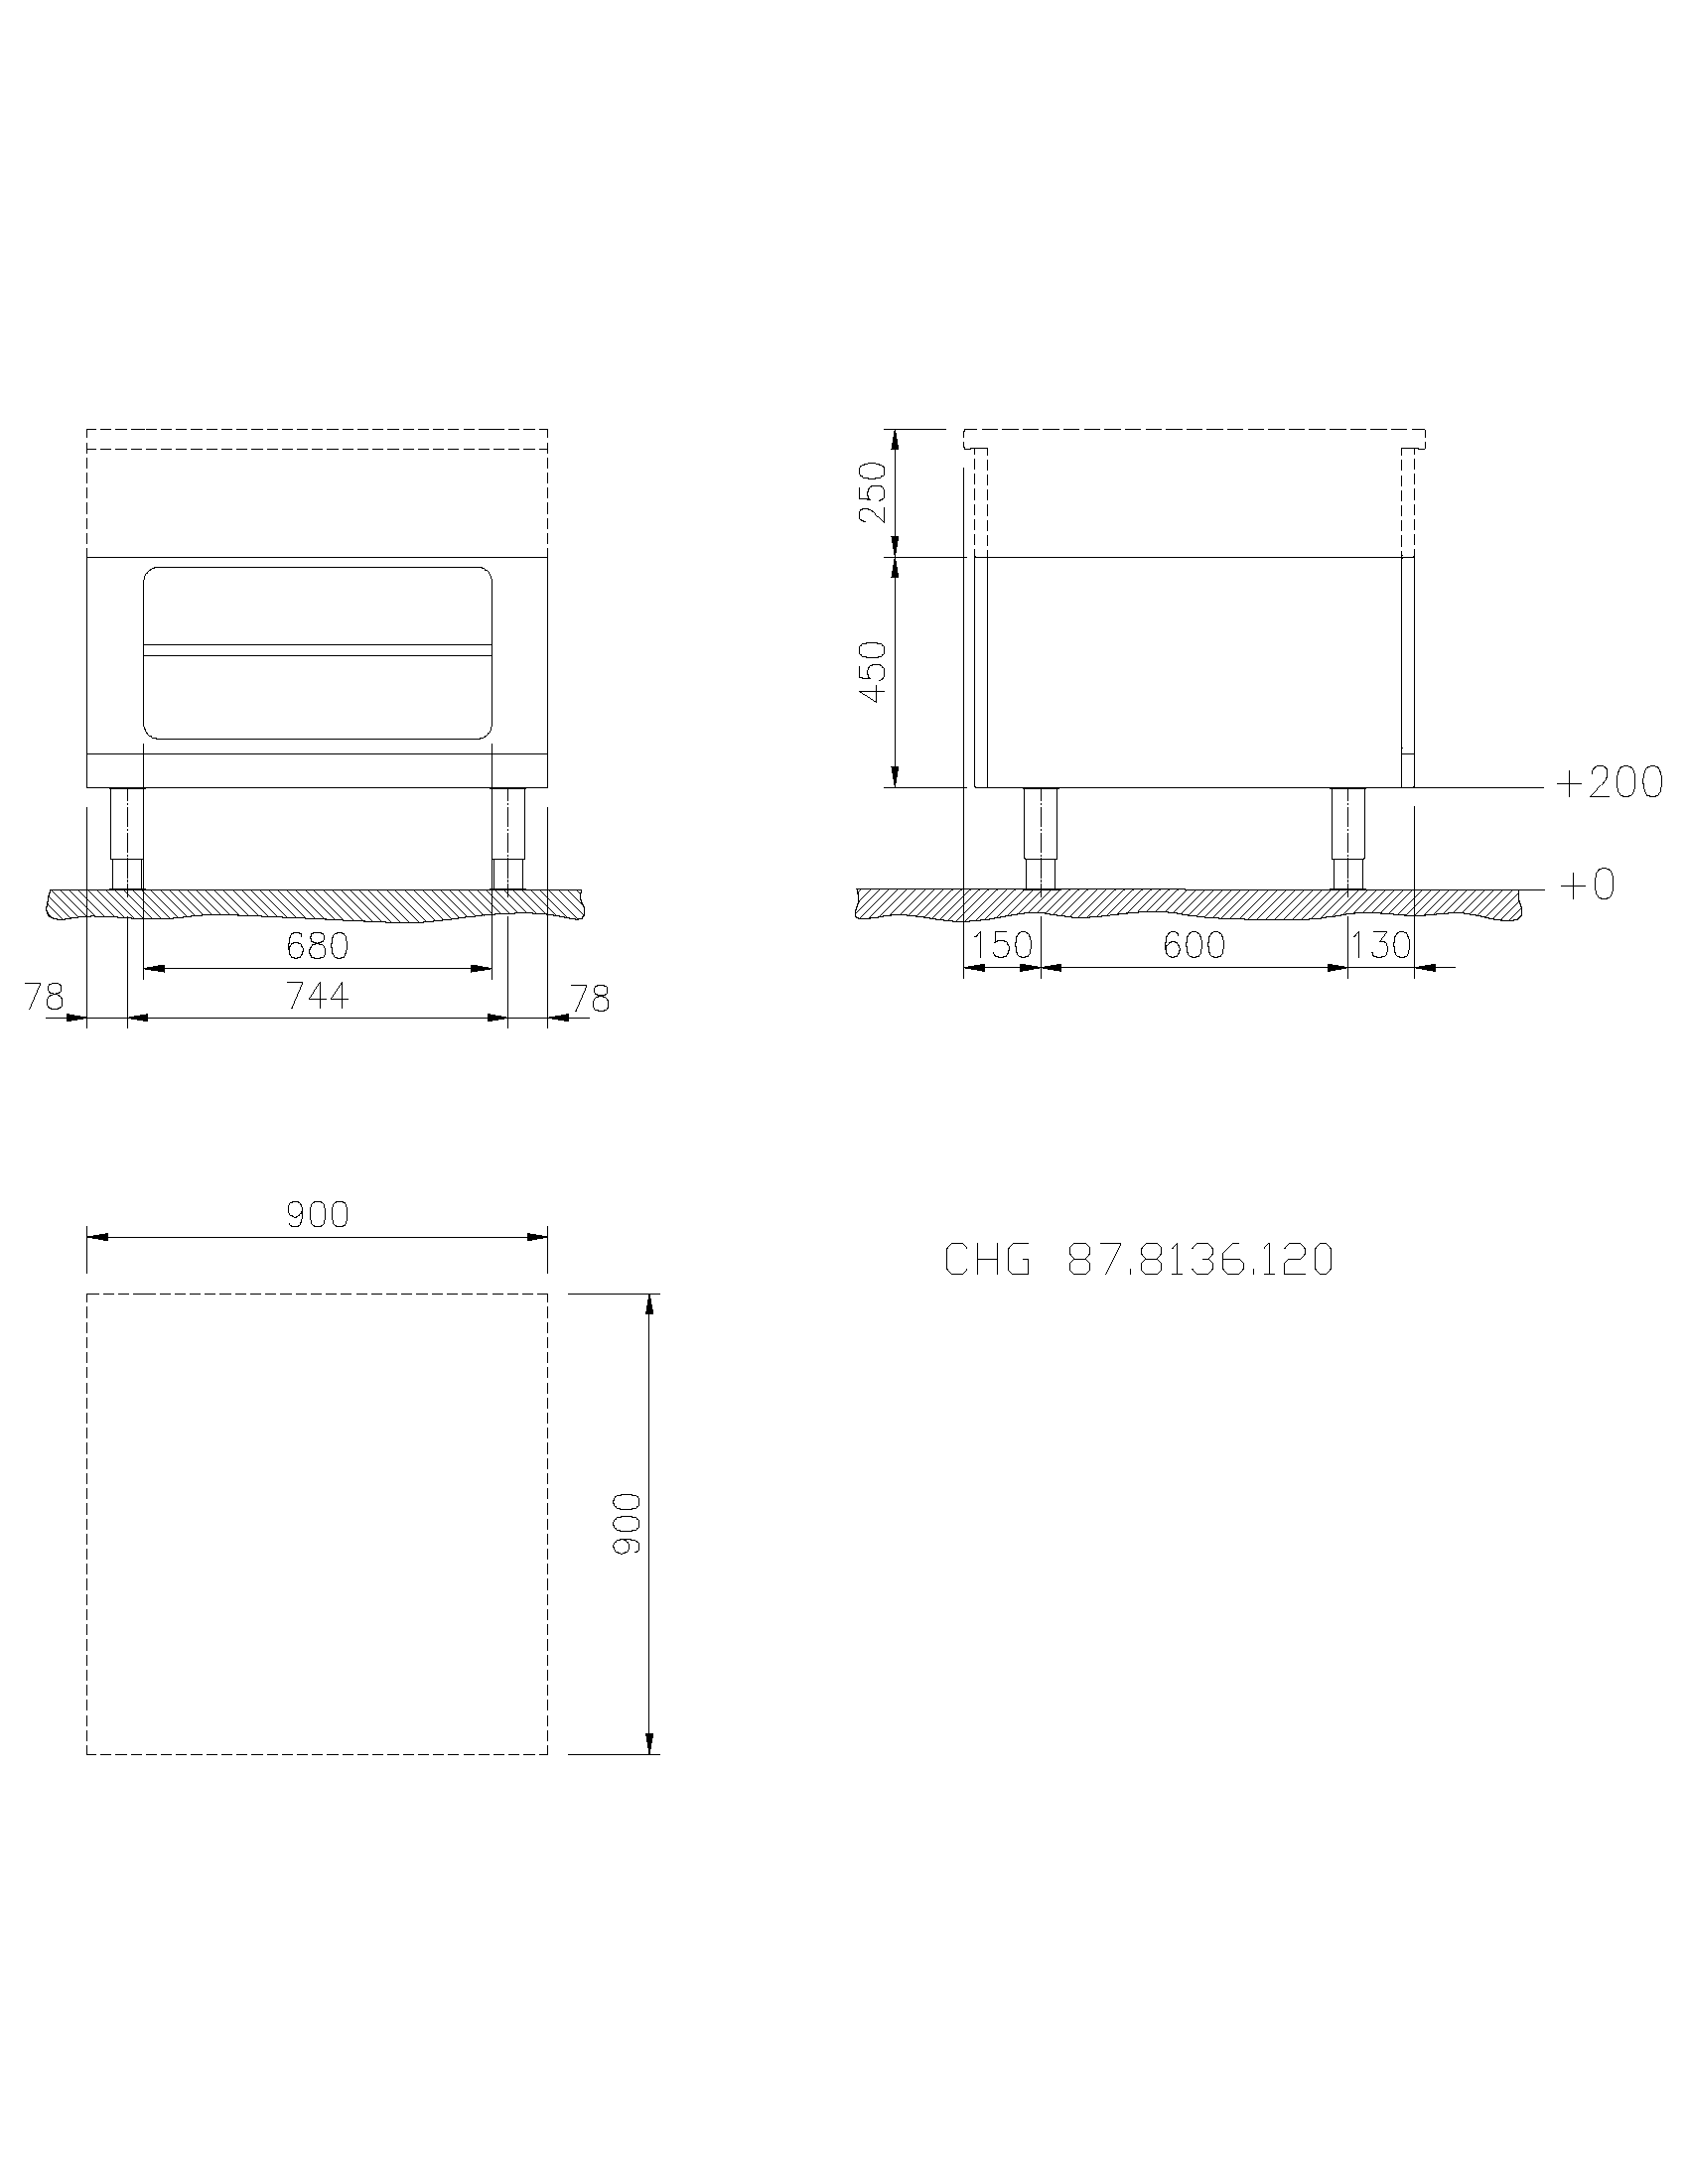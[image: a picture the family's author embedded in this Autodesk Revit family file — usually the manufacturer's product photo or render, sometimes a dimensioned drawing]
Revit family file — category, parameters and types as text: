
# Revit family: QF_ELECTROLUXPROFESSIONAL_589838_MCHZEAD1DM
name_source: partatom
category: Attrezzature speciali
units: mm (PartAtom-declared; Revit-internal decimal feet)

## family parameters
Basato su piano di lavoro = No
Condiviso = No
Punto di calcolo locali = No
Quota connettore circolare = Usa diametro
Sempre verticale = Sì
Taglio con vuoti quando caricato = No
Tipo di parte = Normale

## types (1)
- Standard
    Accessory = Sì
    Cold Water Size = 0"
    Compressed Air Pressure = 0.00 psi
    Compressed Air Size = 0"
    Compressed Air Volume = 0 GPM
    Condensate Return Size = 0"
    Cycle = 50 Hz
    Depth Actual = 900 mm  [stored 2.95276 ft]
    Descrizione = FRYTOP,H3,RBD,1Z,1S,400X900X700H MARINE
    Direct Waste Size = 0"
    Gas Input Pressure = 0.0
    Gas KW = 0
    Gas Size = 0"
    HP = 6.8 HP
    Height Actual = 700 mm  [stored 2.29659 ft]
    Hot Water Size = 0"
    Item Number = 589838
    Length Actual = 400 mm  [stored 1.31234 ft]
    Modello = MCHZEAD1DM
    Phase = 3
    Produttore = Electrolux Professional
    Prospetto di default = 0 mm  [stored 0 ft]
    Refrigerant Compressor Remote = Sì
    Refrigeration Liquid Line Size = 0 mm  [stored 0 ft]
    Refrigeration Suction Line Size = 0 mm  [stored 0 ft]
    Steam Consumption per Hour = 0
    Steam Supply Maximum Pressure = 0.00 psi
    Steam Supply Minimum Pressure = 0.00 psi
    Steam Supply Size = 0"
    URL = https://www.electroluxprofessional.com
    URL Manufacturer = https://www.electroluxprofessional.com
    Volts = 440 V
    Watts = 5100 W
    Weight = 91.00 kg

note: source unit labels omitted for Gas Input Pressure — the stored unit's dimension contradicts the parameter name (converter mislabeling)

note: [stored X ft] marks values corroborated as IEEE doubles in the binary element streams (Revit-internal decimal feet)

## geometry (parser evidence)
native form markers: Blend x14, Sweep x12
no freeform markers — native parametric forms only
